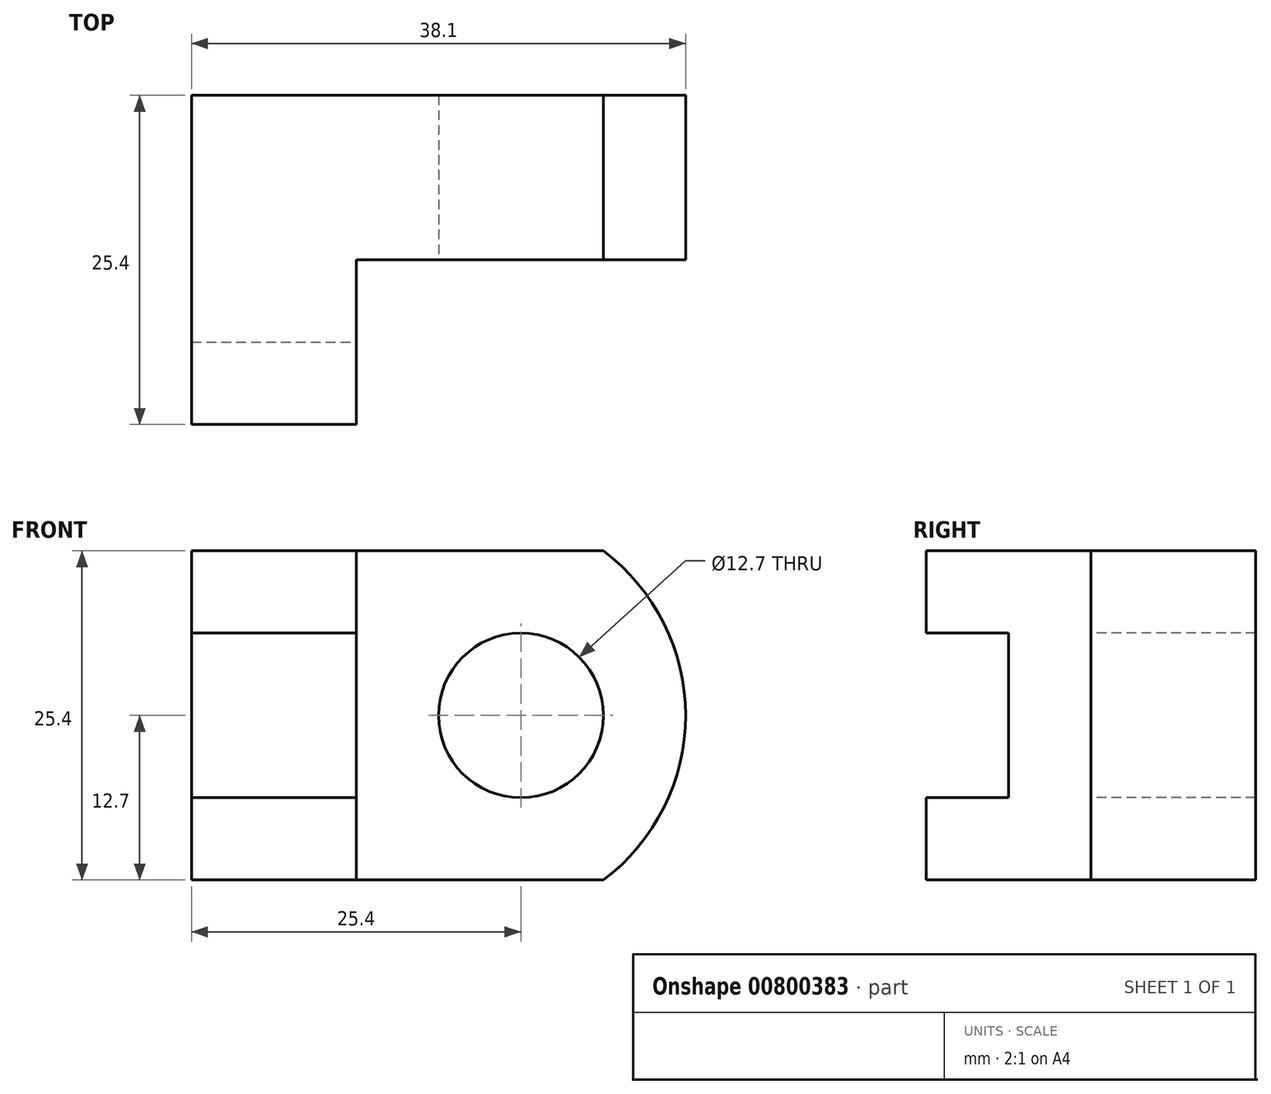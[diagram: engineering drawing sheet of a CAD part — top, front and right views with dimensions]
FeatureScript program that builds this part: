
annotation { "Feature Type Name" : "Feature", "Feature Type Description" : "" }
export const myFeature = defineFeature(function(context is Context, id is Id, definition is map)
    precondition{}
    {
        {
            var Q0;
            Q0=qCreatedBy(makeId("Front.planeOp"),FACE);
            var sketch = newSketch(context, id + "F0", { "sketchPlane" : qUnion([Q0])});
            skLineSegment(sketch, "E0", {"start": v(0, 0) * mm, "end": v(12.7, 0) * mm});
            skLineSegment(sketch, "E1", {"start": v(12.7, 0) * mm, "end": v(12.7, -25.4) * mm});
            skLineSegment(sketch, "E2", {"start": v(12.7, -25.4) * mm, "end": v(0, -25.4) * mm});
            skLineSegment(sketch, "E3", {"start": v(0, 0) * mm, "end": v(0, -25.4) * mm});
            skSolve(sketch);
        }
        {
            var Q0;
            Q0=makeQuery(id+"F0.imprint","IMPRINT",FACE,{"disambiguationData":[TD([[makeQuery(id+"F0.imprint","IMPRINT",EDGE,{"derivedFrom":sQuery(id+"F0.wireOp",EDGE,"E0")}),-1.0]])]});
            extrude(context, id + "F1", {"entities" : qUnion([Q0]), "depth" : 25.4 * mm, "offsetDistance" : 25.4 * mm});
        }
        {
            var Q0;
            Q0=makeQuery(id+"F1.opExtrude","CAP_FACE",FACE,{"disambiguationData":[OSD([sQuery(id+"F0.wireOp",EDGE,"E0"),sQuery(id+"F0.wireOp",EDGE,"E1"),sQuery(id+"F0.wireOp",EDGE,"E2"),sQuery(id+"F0.wireOp",EDGE,"E3")])],"isStart":false});
            var sketch = newSketch(context, id + "F2", { "sketchPlane" : qUnion([Q0])});
            skLineSegment(sketch, "E4", {"start": v(0, -25.4) * mm, "end": v(0, -19.05) * mm});
            skLineSegment(sketch, "E5", {"start": v(0, 0) * mm, "end": v(0, -6.35) * mm});
            skLineSegment(sketch, "E6", {"start": v(0, -6.35) * mm, "end": v(12.7, -6.35) * mm});
            skLineSegment(sketch, "E7", {"start": v(0, -19.05) * mm, "end": v(12.7, -19.05) * mm});
            skSolve(sketch);
        }
        {
            var Q0;
            {var subQ0=sQuery(id+"F2.wireOp",EDGE,"E6");Q0=makeQuery(id+"F2.imprint","IMPRINT",FACE,{"disambiguationData":[TD([[makeQuery(id+"F2.imprint","IMPRINT",EDGE,{"derivedFrom":subQ0}),-1.0]])]});}
            extrude(context, id + "F3", {"entities" : qUnion([Q0]), "operationType" : NewBodyOperationType.REMOVE, "oppositeDirection" : true, "depth" : 6.35 * mm, "offsetDistance" : 25.4 * mm});
        }
        {
            var Q0;
            Q0=makeQuery(id+"F1.opExtrude","SWEPT_FACE",FACE,{"disambiguationData":[OSD([sQuery(id+"F0.wireOp",EDGE,"E1")])]});
            var sketch = newSketch(context, id + "F4", { "sketchPlane" : qUnion([Q0])});
            skLineSegment(sketch, "E8", {"start": v(-25.4, -25.4) * mm, "end": v(-12.7, -25.4) * mm});
            skLineSegment(sketch, "E9", {"start": v(-12.7, -25.4) * mm, "end": v(-12.7, 0) * mm});
            skSolve(sketch);
        }
        {
            var Q0;
            {var subQ0=sQuery(id+"F4.wireOp",EDGE,"E9");Q0=makeQuery(id+"F4.imprint","IMPRINT",FACE,{"disambiguationData":[TD([[makeQuery(id+"F4.imprint","IMPRINT",EDGE,{"derivedFrom":subQ0}),-1.0]])]});}
            extrude(context, id + "F5", {"entities" : qUnion([Q0]), "operationType" : NewBodyOperationType.ADD, "depth" : 25.4 * mm, "offsetDistance" : 25.4 * mm});
        }
        {
            var Q0;
            Q0=makeQuery(id+"F5.opExtrude","SWEPT_FACE",FACE,{"disambiguationData":[OSD([sQuery(id+"F4.wireOp",EDGE,"E9")])]});
            var sketch = newSketch(context, id + "F6", { "sketchPlane" : qUnion([Q0])});
            skArc(sketch, "E10", {"start": v(12.7, -25.4) * mm, "mid": v(38.1, -12.7) * mm, "end": v(12.7, 0) * mm});
            skSolve(sketch);
        }
        {
            var Q0;
            {var subQ0=sQuery(id+"F6.wireOp",EDGE,"E10");var subQ1=sQuery(id+"F4.wireOp",EDGE,"E9");var subQ2=makeQuery(id+"F5.opExtrude","CAP_EDGE",EDGE,{"disambiguationData":[OSD([subQ1])],"isStart":false});var subQ3=makeQuery(id+"F6.imprint","INTERSECT",VERTEX,{"derivedFrom":[subQ2,subQ0]});Q0=makeQuery(id+"F6.imprint","IMPRINT",FACE,{"disambiguationData":[TD([[makeQuery(id+"F6.imprint","IMPRINT",EDGE,{"disambiguationData":[TD([[subQ3,-1.0]])],"derivedFrom":subQ0}),-1.0]])]});}
            var Q1;
            {var subQ0=sQuery(id+"F6.wireOp",EDGE,"E10");var subQ1=sQuery(id+"F4.wireOp",EDGE,"E9");var subQ4=makeQuery(id+"F5.opExtrude","CAP_EDGE",EDGE,{"disambiguationData":[OSD([subQ1])],"isStart":false});var subQ5=makeQuery(id+"F6.imprint","INTERSECT",VERTEX,{"derivedFrom":[subQ4,subQ0]});Q1=makeQuery(id+"F6.imprint","IMPRINT",FACE,{"disambiguationData":[TD([[makeQuery(id+"F6.imprint","IMPRINT",EDGE,{"disambiguationData":[TD([[subQ5,1.0]])],"derivedFrom":subQ0}),-1.0]])]});}
            extrude(context, id + "F7", {"entities" : qUnion([Q0, Q1]), "operationType" : NewBodyOperationType.REMOVE, "endBound" : BoundingType.THROUGH_ALL, "oppositeDirection" : true, "depth" : 25.4 * mm, "offsetDistance" : 25.4 * mm});
        }
        {
            var Q0;
            Q0=makeQuery(id+"F5.opExtrude","SWEPT_FACE",FACE,{"disambiguationData":[OSD([sQuery(id+"F4.wireOp",EDGE,"E9")])]});
            var sketch = newSketch(context, id + "F8", { "sketchPlane" : qUnion([Q0])});
            skLineSegment(sketch, "E11", {"start": v(12.7, -12.7) * mm, "end": v(25.4, -12.7) * mm, "construction": true});
            skLineSegment(sketch, "E12", {"start": v(38.1, -12.7) * mm, "end": v(25.4, -12.7) * mm, "construction": true});
            skCircle(sketch, "E13", {"center": v(25.4, -12.7) * mm, "radius": 6.35 * mm});
            skSolve(sketch);
        }
        {
            var Q0;
            Q0=makeQuery(id+"F8.imprint","IMPRINT",FACE,{"disambiguationData":[TD([[makeQuery(id+"F8.imprint","IMPRINT",EDGE,{"derivedFrom":sQuery(id+"F8.wireOp",EDGE,"E13")}),1.0]])]});
            extrude(context, id + "F9", {"entities" : qUnion([Q0]), "operationType" : NewBodyOperationType.REMOVE, "endBound" : BoundingType.THROUGH_ALL, "oppositeDirection" : true, "depth" : 25.4 * mm, "offsetDistance" : 25.4 * mm});
        }
    });
